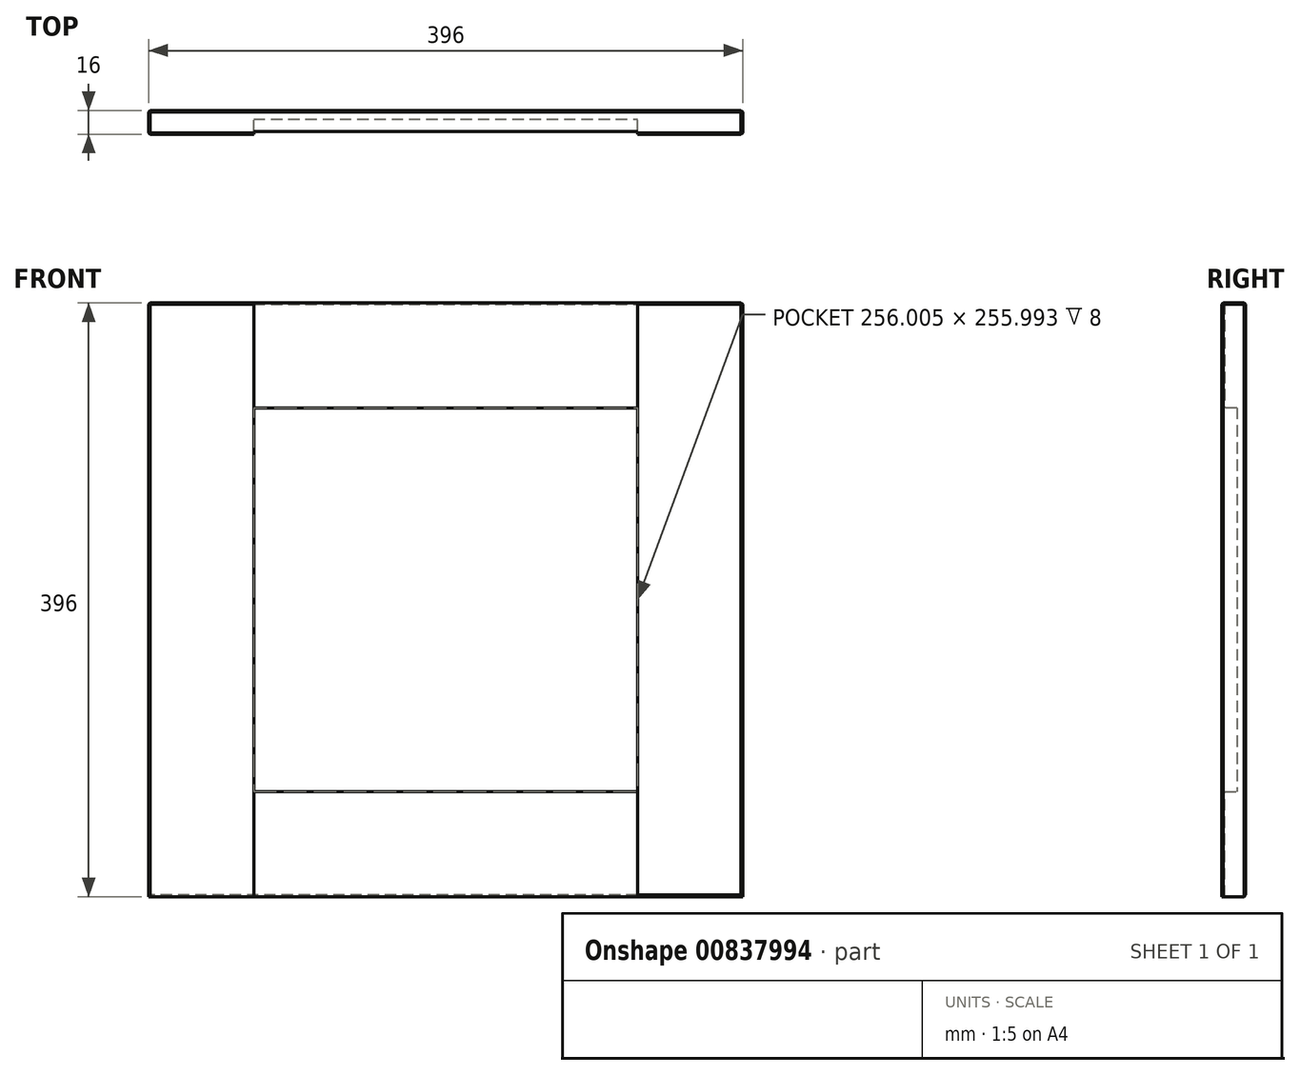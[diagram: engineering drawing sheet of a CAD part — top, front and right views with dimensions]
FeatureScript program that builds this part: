
annotation { "Feature Type Name" : "Feature", "Feature Type Description" : "" }
export const myFeature = defineFeature(function(context is Context, id is Id, definition is map)
    precondition{}
    {
        {
            var Q0;
            Q0=qCreatedBy(makeId("Front.planeOp"),FACE);
            var sketch = newSketch(context, id + "F0", { "sketchPlane" : qUnion([Q0])});
            skLineSegment(sketch, "E0.bottom", {"start": v(0, 0) * mm, "end": v(35.9, 0) * mm});
            skLineSegment(sketch, "E0.top", {"start": v(0, 30.12) * mm, "end": v(35.9, 30.12) * mm});
            skLineSegment(sketch, "E0.left", {"start": v(0, 0) * mm, "end": v(0, 30.12) * mm});
            skLineSegment(sketch, "E0.right", {"start": v(35.9, 0) * mm, "end": v(35.9, 30.12) * mm});
            skSolve(sketch);
        }
        {
            var Q0;
            Q0=makeQuery(id+"F0.imprint","IMPRINT",FACE,{"disambiguationData":[TD([[makeQuery(id+"F0.imprint","IMPRINT",EDGE,{"derivedFrom":sQuery(id+"F0.wireOp",EDGE,"E0.bottom")}),1.0]])]});
            extrude(context, id + "F1", {"entities" : qUnion([Q0]), "depth" : 16 * mm, "offsetDistance" : 25.4 * mm});
        }
        {
            var Q0;
            Q0=makeQuery(id+"F1.opExtrude","SWEPT_FACE",FACE,{"disambiguationData":[OSD([sQuery(id+"F0.wireOp",EDGE,"E0.left")])]});
            extrude(context, id + "F2", {"entities" : qUnion([Q0]), "operationType" : NewBodyOperationType.ADD, "oppositeDirection" : true, "depth" : 196 * mm, "offsetDistance" : 25 * mm});
        }
        {
            var Q0;
            {var subQ0=sQuery(id+"F0.wireOp",EDGE,"E0.bottom");Q0=makeQuery(id+"F2.boolean.opBoolean","MERGE",FACE,{"derivedFrom":[makeQuery(id+"F1.opExtrude","SWEPT_FACE",FACE,{"disambiguationData":[OSD([subQ0])]}),makeQuery(id+"F2.opExtrude","SWEPT_FACE",FACE,{"disambiguationData":[OSD([subQ0,sQuery(id+"F0.wireOp",EDGE,"E0.left")])]})]});}
            extrude(context, id + "F3", {"entities" : qUnion([Q0]), "operationType" : NewBodyOperationType.ADD, "oppositeDirection" : true, "depth" : 796 * mm, "offsetDistance" : 25 * mm});
        }
        {
            var Q0;
            {var subQ0=sQuery(id+"F0.wireOp",EDGE,"E0.left");var subQ1=sQuery(id+"F0.wireOp",EDGE,"E0.bottom");Q0=makeQuery(id+"F3.boolean.opBoolean","MERGE",FACE,{"derivedFrom":[makeQuery(id+"F2.boolean.opBoolean","MERGE",FACE,{"derivedFrom":[makeQuery(id+"F1.opExtrude","CAP_FACE",FACE,{"disambiguationData":[OSD([subQ1,sQuery(id+"F0.wireOp",EDGE,"E0.top"),subQ0,sQuery(id+"F0.wireOp",EDGE,"E0.right")])],"isStart":false}),makeQuery(id+"F2.opExtrude","SWEPT_FACE",FACE,{"disambiguationData":[OSD([subQ0]),TDD([makeQuery(id+"F1.opExtrude","CAP_EDGE",EDGE,{"disambiguationData":[OSD([subQ0])],"isStart":false})])]})]}),makeQuery(id+"F3.opExtrude","SWEPT_FACE",FACE,{"disambiguationData":[OSD([subQ1,subQ0]),TDD([makeQuery(id+"F2.boolean.opBoolean","MERGE",EDGE,{"derivedFrom":[makeQuery(id+"F1.opExtrude","CAP_EDGE",EDGE,{"disambiguationData":[OSD([subQ1])],"isStart":false}),makeQuery(id+"F2.opExtrude","SWEPT_EDGE",EDGE,{"disambiguationData":[OSD([subQ1,subQ0]),TDD([makeQuery(id+"F1.opExtrude","CAP_VERTEX",VERTEX,{"disambiguationData":[OSD([subQ1,subQ0])],"isStart":false})])]})]})])]})]});}
            var sketch = newSketch(context, id + "F4", { "sketchPlane" : qUnion([Q0])});
            skLineSegment(sketch, "E1.bottom", {"start": v(0, 796) * mm, "end": v(42.19, 796) * mm});
            skLineSegment(sketch, "E1.top", {"start": v(0, 751.57) * mm, "end": v(42.19, 751.57) * mm});
            skLineSegment(sketch, "E1.left", {"start": v(0, 796) * mm, "end": v(0, 751.57) * mm});
            skLineSegment(sketch, "E1.right", {"start": v(42.19, 796) * mm, "end": v(42.19, 751.57) * mm});
            skLineSegment(sketch, "E2.bottom", {"start": v(196, 796) * mm, "end": v(153.6, 796) * mm});
            skLineSegment(sketch, "E2.top", {"start": v(196, 746.75) * mm, "end": v(153.6, 746.75) * mm});
            skLineSegment(sketch, "E2.left", {"start": v(196, 796) * mm, "end": v(196, 746.75) * mm});
            skLineSegment(sketch, "E2.right", {"start": v(153.6, 796) * mm, "end": v(153.6, 746.75) * mm});
            skSolve(sketch);
        }
        {
            var Q0;
            Q0=makeQuery(id+"F4.imprint","IMPRINT",FACE,{"disambiguationData":[TD([[makeQuery(id+"F4.imprint","IMPRINT",EDGE,{"derivedFrom":sQuery(id+"F4.wireOp",EDGE,"E1.bottom")}),-1.0]])]});
            var Q1;
            Q1=makeQuery(id+"F4.imprint","IMPRINT",FACE,{"disambiguationData":[TD([[makeQuery(id+"F4.imprint","IMPRINT",EDGE,{"derivedFrom":sQuery(id+"F4.wireOp",EDGE,"E2.bottom")}),-1.0]])]});
            extrude(context, id + "F5", {"entities" : qUnion([Q0, Q1]), "operationType" : NewBodyOperationType.ADD, "depth" : 25 * mm, "offsetDistance" : 25 * mm});
        }
        {
            var Q0;
            {var subQ0=sQuery(id+"F0.wireOp",EDGE,"E0.left");var subQ1=sQuery(id+"F0.wireOp",EDGE,"E0.bottom");Q0=makeQuery(id+"F3.boolean.opBoolean","MERGE",FACE,{"derivedFrom":[makeQuery(id+"F2.boolean.opBoolean","MERGE",FACE,{"derivedFrom":[makeQuery(id+"F1.opExtrude","CAP_FACE",FACE,{"disambiguationData":[OSD([subQ1,sQuery(id+"F0.wireOp",EDGE,"E0.top"),subQ0,sQuery(id+"F0.wireOp",EDGE,"E0.right")])],"isStart":false}),makeQuery(id+"F2.opExtrude","SWEPT_FACE",FACE,{"disambiguationData":[OSD([subQ0]),TDD([makeQuery(id+"F1.opExtrude","CAP_EDGE",EDGE,{"disambiguationData":[OSD([subQ0])],"isStart":false})])]})]}),makeQuery(id+"F3.opExtrude","SWEPT_FACE",FACE,{"disambiguationData":[OSD([subQ1,subQ0]),TDD([makeQuery(id+"F2.boolean.opBoolean","MERGE",EDGE,{"derivedFrom":[makeQuery(id+"F1.opExtrude","CAP_EDGE",EDGE,{"disambiguationData":[OSD([subQ1])],"isStart":false}),makeQuery(id+"F2.opExtrude","SWEPT_EDGE",EDGE,{"disambiguationData":[OSD([subQ1,subQ0]),TDD([makeQuery(id+"F1.opExtrude","CAP_VERTEX",VERTEX,{"disambiguationData":[OSD([subQ1,subQ0])],"isStart":false})])]})]})])]})]});}
            var sketch = newSketch(context, id + "F6", { "sketchPlane" : qUnion([Q0])});
            skLineSegment(sketch, "E3.bottom", {"start": v(196, 0) * mm, "end": v(163.38, 0) * mm});
            skLineSegment(sketch, "E3.top", {"start": v(196, 46.55) * mm, "end": v(163.38, 46.55) * mm});
            skLineSegment(sketch, "E3.left", {"start": v(196, 0) * mm, "end": v(196, 46.55) * mm});
            skLineSegment(sketch, "E3.right", {"start": v(163.38, 0) * mm, "end": v(163.38, 46.55) * mm});
            skLineSegment(sketch, "E4.bottom", {"start": v(0, 0) * mm, "end": v(50.28, 0) * mm});
            skLineSegment(sketch, "E4.top", {"start": v(0, 44.4) * mm, "end": v(50.28, 44.4) * mm});
            skLineSegment(sketch, "E4.left", {"start": v(0, 0) * mm, "end": v(0, 44.4) * mm});
            skLineSegment(sketch, "E4.right", {"start": v(50.28, 0) * mm, "end": v(50.28, 44.4) * mm});
            skSolve(sketch);
        }
        {
            var Q0;
            Q0=makeQuery(id+"F6.imprint","IMPRINT",FACE,{"disambiguationData":[TD([[makeQuery(id+"F6.imprint","IMPRINT",EDGE,{"derivedFrom":sQuery(id+"F6.wireOp",EDGE,"E3.bottom")}),1.0]])]});
            var Q1;
            Q1=makeQuery(id+"F6.imprint","IMPRINT",FACE,{"disambiguationData":[TD([[makeQuery(id+"F6.imprint","IMPRINT",EDGE,{"derivedFrom":sQuery(id+"F6.wireOp",EDGE,"E4.bottom")}),1.0]])]});
            extrude(context, id + "F7", {"entities" : qUnion([Q0, Q1]), "operationType" : NewBodyOperationType.ADD, "depth" : 25 * mm, "offsetDistance" : 25 * mm});
        }
        {
            var Q0;
            Q0=makeQuery(id+"F7.opExtrude","SWEPT_FACE",FACE,{"disambiguationData":[OSD([sQuery(id+"F6.wireOp",EDGE,"E4.right")])]});
            extrude(context, id + "F8", {"entities" : qUnion([Q0]), "operationType" : NewBodyOperationType.ADD, "depth" : 19.72 * mm, "offsetDistance" : 25 * mm});
        }
        {
            var Q0;
            {var subQ0=sQuery(id+"F6.wireOp",EDGE,"E4.top");Q0=makeQuery(id+"F8.boolean.opBoolean","MERGE",FACE,{"derivedFrom":[makeQuery(id+"F7.opExtrude","SWEPT_FACE",FACE,{"disambiguationData":[OSD([subQ0])]}),makeQuery(id+"F8.opExtrude","SWEPT_FACE",FACE,{"disambiguationData":[OSD([subQ0,sQuery(id+"F6.wireOp",EDGE,"E4.right")])]})]});}
            extrude(context, id + "F9", {"entities" : qUnion([Q0]), "operationType" : NewBodyOperationType.ADD, "depth" : 25.6 * mm, "offsetDistance" : 25 * mm});
        }
        {
            var Q0;
            Q0=makeQuery(id+"F7.opExtrude","SWEPT_FACE",FACE,{"disambiguationData":[OSD([sQuery(id+"F6.wireOp",EDGE,"E3.right")])]});
            extrude(context, id + "F10", {"entities" : qUnion([Q0]), "operationType" : NewBodyOperationType.ADD, "depth" : 37.38 * mm, "offsetDistance" : 25 * mm});
        }
        {
            var Q0;
            {var subQ0=sQuery(id+"F6.wireOp",EDGE,"E3.top");Q0=makeQuery(id+"F10.boolean.opBoolean","MERGE",FACE,{"derivedFrom":[makeQuery(id+"F7.opExtrude","SWEPT_FACE",FACE,{"disambiguationData":[OSD([subQ0])]}),makeQuery(id+"F10.opExtrude","SWEPT_FACE",FACE,{"disambiguationData":[OSD([subQ0,sQuery(id+"F6.wireOp",EDGE,"E3.right")])]})]});}
            extrude(context, id + "F11", {"entities" : qUnion([Q0]), "operationType" : NewBodyOperationType.ADD, "depth" : 23.45 * mm, "offsetDistance" : 25 * mm});
        }
        {
            var Q0;
            Q0=makeQuery(id+"F5.opExtrude","SWEPT_FACE",FACE,{"disambiguationData":[OSD([sQuery(id+"F4.wireOp",EDGE,"E1.right")])]});
            extrude(context, id + "F12", {"entities" : qUnion([Q0]), "operationType" : NewBodyOperationType.ADD, "depth" : 27.8 * mm, "offsetDistance" : 25 * mm});
        }
        {
            var Q0;
            {var subQ0=sQuery(id+"F4.wireOp",EDGE,"E1.top");Q0=makeQuery(id+"F12.boolean.opBoolean","MERGE",FACE,{"derivedFrom":[makeQuery(id+"F5.opExtrude","SWEPT_FACE",FACE,{"disambiguationData":[OSD([subQ0])]}),makeQuery(id+"F12.opExtrude","SWEPT_FACE",FACE,{"disambiguationData":[OSD([subQ0,sQuery(id+"F4.wireOp",EDGE,"E1.right")])]})]});}
            extrude(context, id + "F13", {"entities" : qUnion([Q0]), "operationType" : NewBodyOperationType.ADD, "depth" : 25.57 * mm, "offsetDistance" : 25 * mm});
        }
        {
            var Q0;
            Q0=makeQuery(id+"F5.opExtrude","SWEPT_FACE",FACE,{"disambiguationData":[OSD([sQuery(id+"F4.wireOp",EDGE,"E2.top")])]});
            extrude(context, id + "F14", {"entities" : qUnion([Q0]), "operationType" : NewBodyOperationType.ADD, "depth" : 20.75 * mm, "offsetDistance" : 25 * mm});
        }
        {
            var Q0;
            {var subQ0=sQuery(id+"F4.wireOp",EDGE,"E2.right");Q0=makeQuery(id+"F14.boolean.opBoolean","MERGE",FACE,{"derivedFrom":[makeQuery(id+"F5.opExtrude","SWEPT_FACE",FACE,{"disambiguationData":[OSD([subQ0])]}),makeQuery(id+"F14.opExtrude","SWEPT_FACE",FACE,{"disambiguationData":[OSD([sQuery(id+"F4.wireOp",EDGE,"E2.top"),subQ0])]})]});}
            extrude(context, id + "F15", {"entities" : qUnion([Q0]), "operationType" : NewBodyOperationType.ADD, "depth" : 27.6 * mm, "offsetDistance" : 25 * mm});
        }
        {
            var Q0;
            {var subQ0=sQuery(id+"F0.wireOp",EDGE,"E0.left");var subQ1=sQuery(id+"F0.wireOp",EDGE,"E0.bottom");Q0=makeQuery(id+"F3.boolean.opBoolean","MERGE",FACE,{"derivedFrom":[makeQuery(id+"F2.boolean.opBoolean","MERGE",FACE,{"derivedFrom":[makeQuery(id+"F1.opExtrude","CAP_FACE",FACE,{"disambiguationData":[OSD([subQ1,sQuery(id+"F0.wireOp",EDGE,"E0.top"),subQ0,sQuery(id+"F0.wireOp",EDGE,"E0.right")])],"isStart":false}),makeQuery(id+"F2.opExtrude","SWEPT_FACE",FACE,{"disambiguationData":[OSD([subQ0]),TDD([makeQuery(id+"F1.opExtrude","CAP_EDGE",EDGE,{"disambiguationData":[OSD([subQ0])],"isStart":false})])]})]}),makeQuery(id+"F3.opExtrude","SWEPT_FACE",FACE,{"disambiguationData":[OSD([subQ1,subQ0]),TDD([makeQuery(id+"F2.boolean.opBoolean","MERGE",EDGE,{"derivedFrom":[makeQuery(id+"F1.opExtrude","CAP_EDGE",EDGE,{"disambiguationData":[OSD([subQ1])],"isStart":false}),makeQuery(id+"F2.opExtrude","SWEPT_EDGE",EDGE,{"disambiguationData":[OSD([subQ1,subQ0]),TDD([makeQuery(id+"F1.opExtrude","CAP_VERTEX",VERTEX,{"disambiguationData":[OSD([subQ1,subQ0])],"isStart":false})])]})]})])]})]});}
            var sketch = newSketch(context, id + "F16", { "sketchPlane" : qUnion([Q0])});
            skLineSegment(sketch, "E5.bottom", {"start": v(70, 726) * mm, "end": v(126, 726) * mm});
            skLineSegment(sketch, "E5.top", {"start": v(70, 70) * mm, "end": v(126, 70) * mm});
            skLineSegment(sketch, "E5.left", {"start": v(70, 726) * mm, "end": v(70, 70) * mm});
            skLineSegment(sketch, "E5.right", {"start": v(126, 726) * mm, "end": v(126, 70) * mm});
            skSolve(sketch);
        }
        {
            var Q0;
            Q0=makeQuery(id+"F16.imprint","IMPRINT",FACE,{"disambiguationData":[TD([[makeQuery(id+"F16.imprint","IMPRINT",EDGE,{"derivedFrom":sQuery(id+"F16.wireOp",EDGE,"E5.top")}),1.0]])]});
            extrude(context, id + "F17", {"entities" : qUnion([Q0]), "operationType" : NewBodyOperationType.REMOVE, "oppositeDirection" : true, "depth" : 10 * mm, "offsetDistance" : 25 * mm});
        }
        {
            var Q0;
            {var subQ2=sQuery(id+"F0.wireOp",EDGE,"E0.left");var subQ3=sQuery(id+"F0.wireOp",EDGE,"E0.bottom");var subQ4=makeQuery(id+"F1.opExtrude","CAP_FACE",FACE,{"disambiguationData":[OSD([subQ3,sQuery(id+"F0.wireOp",EDGE,"E0.top"),subQ2,sQuery(id+"F0.wireOp",EDGE,"E0.right")])],"isStart":false});var subQ7=makeQuery(id+"F3.opExtrude","SWEPT_FACE",FACE,{"disambiguationData":[OSD([subQ3,subQ2]),TDD([makeQuery(id+"F2.boolean.opBoolean","MERGE",EDGE,{"derivedFrom":[makeQuery(id+"F1.opExtrude","CAP_EDGE",EDGE,{"disambiguationData":[OSD([subQ3])],"isStart":false}),makeQuery(id+"F2.opExtrude","SWEPT_EDGE",EDGE,{"disambiguationData":[OSD([subQ3,subQ2]),TDD([makeQuery(id+"F1.opExtrude","CAP_VERTEX",VERTEX,{"disambiguationData":[OSD([subQ3,subQ2])],"isStart":false})])]})]})])]});var subQ8=makeQuery(id+"F2.opExtrude","SWEPT_FACE",FACE,{"disambiguationData":[OSD([subQ2]),TDD([makeQuery(id+"F1.opExtrude","CAP_EDGE",EDGE,{"disambiguationData":[OSD([subQ2])],"isStart":false})])]});Q0=makeQuery(id+"F17.boolean.opBoolean","SPLIT",FACE,{"disambiguationData":[TD([makeQuery(id+"F1.opExtrude","SWEPT_FACE",FACE,{"disambiguationData":[OSD([subQ3])]})])],"derivedFrom":makeQuery(id+"F3.boolean.opBoolean","MERGE",FACE,{"derivedFrom":[makeQuery(id+"F2.boolean.opBoolean","MERGE",FACE,{"derivedFrom":[subQ4,subQ8]}),subQ7]})});}
            var Q1;
            {var subQ2=sQuery(id+"F4.wireOp",EDGE,"E1.bottom");var subQ3=sQuery(id+"F0.wireOp",EDGE,"E0.left");var subQ4=sQuery(id+"F0.wireOp",EDGE,"E0.bottom");var subQ6=makeQuery(id+"F1.opExtrude","CAP_FACE",FACE,{"disambiguationData":[OSD([subQ4,sQuery(id+"F0.wireOp",EDGE,"E0.top"),subQ3,sQuery(id+"F0.wireOp",EDGE,"E0.right")])],"isStart":false});var subQ7=makeQuery(id+"F2.opExtrude","SWEPT_FACE",FACE,{"disambiguationData":[OSD([subQ3]),TDD([makeQuery(id+"F1.opExtrude","CAP_EDGE",EDGE,{"disambiguationData":[OSD([subQ3])],"isStart":false})])]});var subQ8=makeQuery(id+"F3.opExtrude","SWEPT_FACE",FACE,{"disambiguationData":[OSD([subQ4,subQ3]),TDD([makeQuery(id+"F2.boolean.opBoolean","MERGE",EDGE,{"derivedFrom":[makeQuery(id+"F1.opExtrude","CAP_EDGE",EDGE,{"disambiguationData":[OSD([subQ4])],"isStart":false}),makeQuery(id+"F2.opExtrude","SWEPT_EDGE",EDGE,{"disambiguationData":[OSD([subQ4,subQ3]),TDD([makeQuery(id+"F1.opExtrude","CAP_VERTEX",VERTEX,{"disambiguationData":[OSD([subQ4,subQ3])],"isStart":false})])]})]})])]});Q1=makeQuery(id+"F17.boolean.opBoolean","SPLIT",FACE,{"disambiguationData":[TD([makeQuery(id+"F5.opExtrude","SWEPT_FACE",FACE,{"disambiguationData":[OSD([subQ2])]})])],"derivedFrom":makeQuery(id+"F3.boolean.opBoolean","MERGE",FACE,{"derivedFrom":[makeQuery(id+"F2.boolean.opBoolean","MERGE",FACE,{"derivedFrom":[subQ6,subQ7]}),subQ8]})});}
            extrude(context, id + "F18", {"entities" : qUnion([Q0, Q1]), "operationType" : NewBodyOperationType.REMOVE, "oppositeDirection" : true, "depth" : 2 * mm, "offsetDistance" : 25 * mm});
        }
        {
            var Q0;
            {var subQ0=sQuery(id+"F4.wireOp",EDGE,"E1.right");var subQ1=sQuery(id+"F4.wireOp",EDGE,"E1.top");Q0=makeQuery(id+"F13.boolean.opBoolean","MERGE",FACE,{"derivedFrom":[makeQuery(id+"F12.boolean.opBoolean","MERGE",FACE,{"derivedFrom":[makeQuery(id+"F5.opExtrude","CAP_FACE",FACE,{"disambiguationData":[OSD([sQuery(id+"F4.wireOp",EDGE,"E1.bottom"),subQ1,sQuery(id+"F4.wireOp",EDGE,"E1.left"),subQ0])],"isStart":false}),makeQuery(id+"F12.opExtrude","SWEPT_FACE",FACE,{"disambiguationData":[OSD([subQ0]),TDD([makeQuery(id+"F5.opExtrude","CAP_EDGE",EDGE,{"disambiguationData":[OSD([subQ0])],"isStart":false})])]})]}),makeQuery(id+"F13.opExtrude","SWEPT_FACE",FACE,{"disambiguationData":[OSD([subQ1,subQ0]),TDD([makeQuery(id+"F12.boolean.opBoolean","MERGE",EDGE,{"derivedFrom":[makeQuery(id+"F5.opExtrude","CAP_EDGE",EDGE,{"disambiguationData":[OSD([subQ1])],"isStart":false}),makeQuery(id+"F12.opExtrude","SWEPT_EDGE",EDGE,{"disambiguationData":[OSD([subQ1,subQ0]),TDD([makeQuery(id+"F5.opExtrude","CAP_VERTEX",VERTEX,{"disambiguationData":[OSD([subQ1,subQ0])],"isStart":false})])]})]})])]})]});}
            var Q1;
            {var subQ0=sQuery(id+"F4.wireOp",EDGE,"E2.right");var subQ1=sQuery(id+"F4.wireOp",EDGE,"E2.top");Q1=makeQuery(id+"F15.boolean.opBoolean","MERGE",FACE,{"derivedFrom":[makeQuery(id+"F14.boolean.opBoolean","MERGE",FACE,{"derivedFrom":[makeQuery(id+"F5.opExtrude","CAP_FACE",FACE,{"disambiguationData":[OSD([sQuery(id+"F4.wireOp",EDGE,"E2.bottom"),subQ1,sQuery(id+"F4.wireOp",EDGE,"E2.left"),subQ0])],"isStart":false}),makeQuery(id+"F14.opExtrude","SWEPT_FACE",FACE,{"disambiguationData":[OSD([subQ1]),TDD([makeQuery(id+"F5.opExtrude","CAP_EDGE",EDGE,{"disambiguationData":[OSD([subQ1])],"isStart":false})])]})]}),makeQuery(id+"F15.opExtrude","SWEPT_FACE",FACE,{"disambiguationData":[OSD([subQ1,subQ0]),TDD([makeQuery(id+"F14.boolean.opBoolean","MERGE",EDGE,{"derivedFrom":[makeQuery(id+"F5.opExtrude","CAP_EDGE",EDGE,{"disambiguationData":[OSD([subQ0])],"isStart":false}),makeQuery(id+"F14.opExtrude","SWEPT_EDGE",EDGE,{"disambiguationData":[OSD([subQ1,subQ0]),TDD([makeQuery(id+"F5.opExtrude","CAP_VERTEX",VERTEX,{"disambiguationData":[OSD([subQ1,subQ0])],"isStart":false})])]})]})])]})]});}
            var Q2;
            {var subQ0=sQuery(id+"F6.wireOp",EDGE,"E4.right");var subQ1=sQuery(id+"F6.wireOp",EDGE,"E4.top");Q2=makeQuery(id+"F9.boolean.opBoolean","MERGE",FACE,{"derivedFrom":[makeQuery(id+"F8.boolean.opBoolean","MERGE",FACE,{"derivedFrom":[makeQuery(id+"F7.opExtrude","CAP_FACE",FACE,{"disambiguationData":[OSD([sQuery(id+"F6.wireOp",EDGE,"E4.bottom"),subQ1,sQuery(id+"F6.wireOp",EDGE,"E4.left"),subQ0])],"isStart":false}),makeQuery(id+"F8.opExtrude","SWEPT_FACE",FACE,{"disambiguationData":[OSD([subQ0]),TDD([makeQuery(id+"F7.opExtrude","CAP_EDGE",EDGE,{"disambiguationData":[OSD([subQ0])],"isStart":false})])]})]}),makeQuery(id+"F9.opExtrude","SWEPT_FACE",FACE,{"disambiguationData":[OSD([subQ1,subQ0]),TDD([makeQuery(id+"F8.boolean.opBoolean","MERGE",EDGE,{"derivedFrom":[makeQuery(id+"F7.opExtrude","CAP_EDGE",EDGE,{"disambiguationData":[OSD([subQ1])],"isStart":false}),makeQuery(id+"F8.opExtrude","SWEPT_EDGE",EDGE,{"disambiguationData":[OSD([subQ1,subQ0]),TDD([makeQuery(id+"F7.opExtrude","CAP_VERTEX",VERTEX,{"disambiguationData":[OSD([subQ1,subQ0])],"isStart":false})])]})]})])]})]});}
            var Q3;
            {var subQ0=sQuery(id+"F6.wireOp",EDGE,"E3.right");var subQ1=sQuery(id+"F6.wireOp",EDGE,"E3.top");Q3=makeQuery(id+"F11.boolean.opBoolean","MERGE",FACE,{"derivedFrom":[makeQuery(id+"F10.boolean.opBoolean","MERGE",FACE,{"derivedFrom":[makeQuery(id+"F7.opExtrude","CAP_FACE",FACE,{"disambiguationData":[OSD([sQuery(id+"F6.wireOp",EDGE,"E3.bottom"),subQ1,sQuery(id+"F6.wireOp",EDGE,"E3.left"),subQ0])],"isStart":false}),makeQuery(id+"F10.opExtrude","SWEPT_FACE",FACE,{"disambiguationData":[OSD([subQ0]),TDD([makeQuery(id+"F7.opExtrude","CAP_EDGE",EDGE,{"disambiguationData":[OSD([subQ0])],"isStart":false})])]})]}),makeQuery(id+"F11.opExtrude","SWEPT_FACE",FACE,{"disambiguationData":[OSD([subQ1,subQ0]),TDD([makeQuery(id+"F10.boolean.opBoolean","MERGE",EDGE,{"derivedFrom":[makeQuery(id+"F7.opExtrude","CAP_EDGE",EDGE,{"disambiguationData":[OSD([subQ1])],"isStart":false}),makeQuery(id+"F10.opExtrude","SWEPT_EDGE",EDGE,{"disambiguationData":[OSD([subQ1,subQ0]),TDD([makeQuery(id+"F7.opExtrude","CAP_VERTEX",VERTEX,{"disambiguationData":[OSD([subQ1,subQ0])],"isStart":false})])]})]})])]})]});}
            extrude(context, id + "F19", {"entities" : qUnion([Q0, Q1, Q2, Q3]), "operationType" : NewBodyOperationType.REMOVE, "oppositeDirection" : true, "depth" : 25 * mm, "offsetDistance" : 25 * mm});
        }
        {
            var Q0;
            {var subQ0=sQuery(id+"F4.wireOp",EDGE,"E2.left");var subQ1=sQuery(id+"F0.wireOp",EDGE,"E0.left");var subQ2=sQuery(id+"F0.wireOp",EDGE,"E0.bottom");var subQ3=sQuery(id+"F6.wireOp",EDGE,"E3.left");Q0=makeQuery(id+"F14.boolean.opBoolean","MERGE",FACE,{"derivedFrom":[makeQuery(id+"F11.boolean.opBoolean","MERGE",FACE,{"derivedFrom":[makeQuery(id+"F7.boolean.opBoolean","MERGE",FACE,{"derivedFrom":[makeQuery(id+"F5.boolean.opBoolean","MERGE",FACE,{"derivedFrom":[makeQuery(id+"F3.boolean.opBoolean","MERGE",FACE,{"derivedFrom":[makeQuery(id+"F2.opExtrude","CAP_FACE",FACE,{"disambiguationData":[OSD([subQ1])],"isStart":false}),makeQuery(id+"F3.opExtrude","SWEPT_FACE",FACE,{"disambiguationData":[OSD([subQ2,subQ1]),TDD([makeQuery(id+"F2.opExtrude","CAP_EDGE",EDGE,{"disambiguationData":[OSD([subQ2,subQ1])],"isStart":false})])]})]}),makeQuery(id+"F5.opExtrude","SWEPT_FACE",FACE,{"disambiguationData":[OSD([subQ0])]})]}),makeQuery(id+"F7.opExtrude","SWEPT_FACE",FACE,{"disambiguationData":[OSD([subQ3])]})]}),makeQuery(id+"F11.opExtrude","SWEPT_FACE",FACE,{"disambiguationData":[OSD([subQ2,subQ1,sQuery(id+"F6.wireOp",EDGE,"E3.top"),subQ3])]})]}),makeQuery(id+"F14.opExtrude","SWEPT_FACE",FACE,{"disambiguationData":[OSD([subQ2,subQ1,sQuery(id+"F4.wireOp",EDGE,"E2.top"),subQ0])]})]});}
            extrude(context, id + "F20", {"entities" : qUnion([Q0]), "operationType" : NewBodyOperationType.ADD, "depth" : 200 * mm, "offsetDistance" : 25 * mm});
        }
        {
            var Q0;
            {var subQ0=sQuery(id+"F4.wireOp",EDGE,"E2.right");var subQ1=sQuery(id+"F4.wireOp",EDGE,"E2.top");Q0=makeQuery(id+"F18.boolean.opBoolean","MERGE",FACE,{"derivedFrom":[makeQuery(id+"F15.opExtrude","CAP_FACE",FACE,{"disambiguationData":[OSD([subQ1,subQ0])],"isStart":false}),makeQuery(id+"F18.opExtrude","SWEPT_FACE",FACE,{"disambiguationData":[OSD([subQ1,subQ0])]})]});}
            var Q1;
            {var subQ0=sQuery(id+"F6.wireOp",EDGE,"E3.right");var subQ1=sQuery(id+"F6.wireOp",EDGE,"E3.top");Q1=makeQuery(id+"F18.boolean.opBoolean","MERGE",FACE,{"derivedFrom":[makeQuery(id+"F11.boolean.opBoolean","MERGE",FACE,{"derivedFrom":[makeQuery(id+"F10.opExtrude","CAP_FACE",FACE,{"disambiguationData":[OSD([subQ0])],"isStart":false}),makeQuery(id+"F11.opExtrude","SWEPT_FACE",FACE,{"disambiguationData":[OSD([subQ1,subQ0]),TDD([makeQuery(id+"F10.opExtrude","CAP_EDGE",EDGE,{"disambiguationData":[OSD([subQ1,subQ0])],"isStart":false})])]})]}),makeQuery(id+"F17.boolean.opBoolean","COPY",FACE,{"derivedFrom":makeQuery(id+"F17.opExtrude","SWEPT_FACE",FACE,{"disambiguationData":[OSD([sQuery(id+"F16.wireOp",EDGE,"E5.right")])]})}),makeQuery(id+"F18.opExtrude","SWEPT_FACE",FACE,{"disambiguationData":[OSD([subQ1,subQ0])]})]});}
            extrude(context, id + "F21", {"entities" : qUnion([Q0, Q1]), "operationType" : NewBodyOperationType.REMOVE, "oppositeDirection" : true, "depth" : 200 * mm, "offsetDistance" : 25 * mm});
        }
        {
            var Q0;
            {var subQ0=sQuery(id+"F4.wireOp",EDGE,"E2.bottom");var subQ1=sQuery(id+"F0.wireOp",EDGE,"E0.left");var subQ2=sQuery(id+"F0.wireOp",EDGE,"E0.bottom");var subQ3=sQuery(id+"F4.wireOp",EDGE,"E1.bottom");Q0=makeQuery(id+"F20.boolean.opBoolean","MERGE",FACE,{"derivedFrom":[makeQuery(id+"F15.boolean.opBoolean","MERGE",FACE,{"derivedFrom":[makeQuery(id+"F12.boolean.opBoolean","MERGE",FACE,{"derivedFrom":[makeQuery(id+"F5.boolean.opBoolean","MERGE",FACE,{"derivedFrom":[makeQuery(id+"F3.opExtrude","CAP_FACE",FACE,{"disambiguationData":[OSD([subQ2,subQ1])],"isStart":false}),makeQuery(id+"F5.opExtrude","SWEPT_FACE",FACE,{"disambiguationData":[OSD([subQ3])]}),makeQuery(id+"F5.opExtrude","SWEPT_FACE",FACE,{"disambiguationData":[OSD([subQ0])]})]}),makeQuery(id+"F12.opExtrude","SWEPT_FACE",FACE,{"disambiguationData":[OSD([subQ2,subQ1,subQ3,sQuery(id+"F4.wireOp",EDGE,"E1.right")])]})]}),makeQuery(id+"F15.opExtrude","SWEPT_FACE",FACE,{"disambiguationData":[OSD([subQ2,subQ1,subQ0,sQuery(id+"F4.wireOp",EDGE,"E2.right")])]})]}),makeQuery(id+"F20.opExtrude","SWEPT_FACE",FACE,{"disambiguationData":[OSD([subQ2,subQ1,subQ0,sQuery(id+"F4.wireOp",EDGE,"E2.left")])]})]});}
            extrude(context, id + "F22", {"entities" : qUnion([Q0]), "operationType" : NewBodyOperationType.ADD, "depth" : 200 * mm, "offsetDistance" : 25 * mm});
        }
        {
            var Q0;
            Q0=makeQuery(id+"F17.boolean.opBoolean","COPY",FACE,{"derivedFrom":makeQuery(id+"F17.opExtrude","SWEPT_FACE",FACE,{"disambiguationData":[OSD([sQuery(id+"F16.wireOp",EDGE,"E5.bottom")])]})});
            var Q1;
            {var subQ0=sQuery(id+"F16.wireOp",EDGE,"E5.right");var subQ1=sQuery(id+"F16.wireOp",EDGE,"E5.bottom");var subQ2=sQuery(id+"F4.wireOp",EDGE,"E2.right");var subQ3=sQuery(id+"F4.wireOp",EDGE,"E2.top");var subQ4=makeQuery(id+"F17.boolean.opBoolean","COPY",EDGE,{"derivedFrom":makeQuery(id+"F17.opExtrude","SWEPT_EDGE",EDGE,{"disambiguationData":[OSD([subQ3,subQ2,subQ1,subQ0])]})});Q1=makeQuery(id+"F21.boolean.opBoolean","COPY",FACE,{"derivedFrom":makeQuery(id+"F21.opExtrude","SWEPT_FACE",FACE,{"disambiguationData":[OSD([subQ3,subQ2,subQ1,subQ0]),TDD([makeQuery(id+"F18.boolean.opBoolean","MERGE",EDGE,{"derivedFrom":[subQ4,makeQuery(id+"F18.opExtrude","SWEPT_EDGE",EDGE,{"disambiguationData":[OSD([subQ3,subQ2,subQ1,subQ0])]})]}),makeQuery(id+"F18.boolean.opBoolean","SPLIT",EDGE,{"derivedFrom":subQ4})])]})});}
            extrude(context, id + "F23", {"entities" : qUnion([Q0, Q1]), "operationType" : NewBodyOperationType.REMOVE, "oppositeDirection" : true, "depth" : 200 * mm, "offsetDistance" : 25 * mm});
        }
        {
            var Q0;
            Q0=makeQuery(id+"F23.boolean.opBoolean","COPY",FACE,{"derivedFrom":makeQuery(id+"F23.opExtrude","CAP_FACE",FACE,{"disambiguationData":[OSD([sQuery(id+"F16.wireOp",EDGE,"E5.bottom")])],"isStart":false})});
            var Q1;
            Q1=makeQuery(id+"F23.boolean.opBoolean","COPY",FACE,{"derivedFrom":makeQuery(id+"F23.opExtrude","CAP_FACE",FACE,{"disambiguationData":[OSD([sQuery(id+"F4.wireOp",EDGE,"E2.top"),sQuery(id+"F4.wireOp",EDGE,"E2.right"),sQuery(id+"F16.wireOp",EDGE,"E5.bottom"),sQuery(id+"F16.wireOp",EDGE,"E5.right")])],"isStart":false})});
            extrude(context, id + "F24", {"entities" : qUnion([Q0, Q1]), "operationType" : NewBodyOperationType.ADD, "depth" : 600 * mm, "offsetDistance" : 25 * mm});
        }
        {
            var Q0;
            Q0=makeQuery(id+"F22.opExtrude","CAP_FACE",FACE,{"disambiguationData":[OSD([sQuery(id+"F0.wireOp",EDGE,"E0.bottom"),sQuery(id+"F0.wireOp",EDGE,"E0.left"),sQuery(id+"F4.wireOp",EDGE,"E1.bottom"),sQuery(id+"F4.wireOp",EDGE,"E1.right"),sQuery(id+"F4.wireOp",EDGE,"E2.bottom"),sQuery(id+"F4.wireOp",EDGE,"E2.left"),sQuery(id+"F4.wireOp",EDGE,"E2.right")])],"isStart":false});
            extrude(context, id + "F25", {"entities" : qUnion([Q0]), "operationType" : NewBodyOperationType.REMOVE, "oppositeDirection" : true, "depth" : 600 * mm, "offsetDistance" : 25 * mm, "hasDraft" : true, "draftAngle" : 3 * degree});
        }
        {
            var Q0;
            {var subQ0=sQuery(id+"F4.wireOp",EDGE,"E1.right");var subQ1=sQuery(id+"F4.wireOp",EDGE,"E1.bottom");var subQ2=sQuery(id+"F0.wireOp",EDGE,"E0.left");var subQ3=sQuery(id+"F0.wireOp",EDGE,"E0.bottom");var subQ4=sQuery(id+"F4.wireOp",EDGE,"E1.left");var subQ5=sQuery(id+"F4.wireOp",EDGE,"E1.top");var subQ6=sQuery(id+"F6.wireOp",EDGE,"E4.right");var subQ7=sQuery(id+"F6.wireOp",EDGE,"E4.left");var subQ8=sQuery(id+"F6.wireOp",EDGE,"E4.top");var subQ9=makeQuery(id+"F1.opExtrude","CAP_FACE",FACE,{"disambiguationData":[OSD([subQ3,sQuery(id+"F0.wireOp",EDGE,"E0.top"),subQ2,sQuery(id+"F0.wireOp",EDGE,"E0.right")])],"isStart":false});var subQ10=makeQuery(id+"F3.opExtrude","SWEPT_FACE",FACE,{"disambiguationData":[OSD([subQ3,subQ2]),TDD([makeQuery(id+"F2.boolean.opBoolean","MERGE",EDGE,{"derivedFrom":[makeQuery(id+"F1.opExtrude","CAP_EDGE",EDGE,{"disambiguationData":[OSD([subQ3])],"isStart":false}),makeQuery(id+"F2.opExtrude","SWEPT_EDGE",EDGE,{"disambiguationData":[OSD([subQ3,subQ2]),TDD([makeQuery(id+"F1.opExtrude","CAP_VERTEX",VERTEX,{"disambiguationData":[OSD([subQ3,subQ2])],"isStart":false})])]})]})])]});var subQ11=makeQuery(id+"F2.opExtrude","SWEPT_FACE",FACE,{"disambiguationData":[OSD([subQ2]),TDD([makeQuery(id+"F1.opExtrude","CAP_EDGE",EDGE,{"disambiguationData":[OSD([subQ2])],"isStart":false})])]});Q0=makeQuery(id+"F25.boolean.opBoolean","INTERSECT",EDGE,{"derivedFrom":[makeQuery(id+"F22.boolean.opBoolean","MERGE",FACE,{"derivedFrom":[makeQuery(id+"F19.boolean.opBoolean","MERGE",FACE,{"derivedFrom":[makeQuery(id+"F17.boolean.opBoolean","SPLIT",FACE,{"disambiguationData":[TD([makeQuery(id+"F1.opExtrude","SWEPT_FACE",FACE,{"disambiguationData":[OSD([subQ2])]})])],"derivedFrom":makeQuery(id+"F3.boolean.opBoolean","MERGE",FACE,{"derivedFrom":[makeQuery(id+"F2.boolean.opBoolean","MERGE",FACE,{"derivedFrom":[subQ9,subQ11]}),subQ10]})}),makeQuery(id+"F19.opExtrude","CAP_FACE",FACE,{"disambiguationData":[OSD([sQuery(id+"F6.wireOp",EDGE,"E4.bottom"),subQ8,subQ7,subQ6])],"isStart":false}),makeQuery(id+"F19.opExtrude","CAP_FACE",FACE,{"disambiguationData":[OSD([subQ1,subQ5,subQ4,subQ0])],"isStart":false})]}),makeQuery(id+"F22.opExtrude","SWEPT_FACE",FACE,{"disambiguationData":[OSD([subQ3,subQ2,subQ1,subQ0]),TDD([makeQuery(id+"F19.boolean.opBoolean","COPY",EDGE,{"derivedFrom":makeQuery(id+"F19.opExtrude","CAP_EDGE",EDGE,{"disambiguationData":[OSD([subQ3,subQ2,subQ1,subQ0])],"isStart":false})})])]})]}),makeQuery(id+"F25.opExtrude","CAP_FACE",FACE,{"disambiguationData":[OSD([subQ3,subQ2,subQ1,subQ0,sQuery(id+"F4.wireOp",EDGE,"E2.bottom"),sQuery(id+"F4.wireOp",EDGE,"E2.left"),sQuery(id+"F4.wireOp",EDGE,"E2.right")])],"isStart":false})]});}
            var Q1;
            {var subQ0=sQuery(id+"F4.wireOp",EDGE,"E1.left");var subQ1=sQuery(id+"F0.wireOp",EDGE,"E0.left");var subQ2=sQuery(id+"F0.wireOp",EDGE,"E0.bottom");Q1=makeQuery(id+"F22.boolean.opBoolean","MERGE",EDGE,{"derivedFrom":[makeQuery(id+"F19.boolean.opBoolean","MERGE",EDGE,{"derivedFrom":[makeQuery(id+"F3.boolean.opBoolean","MERGE",EDGE,{"derivedFrom":[makeQuery(id+"F1.opExtrude","CAP_EDGE",EDGE,{"disambiguationData":[OSD([subQ1])],"isStart":false}),makeQuery(id+"F3.opExtrude","SWEPT_EDGE",EDGE,{"disambiguationData":[OSD([subQ2,subQ1]),TDD([makeQuery(id+"F1.opExtrude","CAP_VERTEX",VERTEX,{"disambiguationData":[OSD([subQ2,subQ1])],"isStart":false})])]})]}),makeQuery(id+"F19.opExtrude","CAP_EDGE",EDGE,{"disambiguationData":[OSD([subQ2,subQ1,sQuery(id+"F6.wireOp",EDGE,"E4.top"),sQuery(id+"F6.wireOp",EDGE,"E4.left")])],"isStart":false}),makeQuery(id+"F19.opExtrude","CAP_EDGE",EDGE,{"disambiguationData":[OSD([subQ2,subQ1,sQuery(id+"F4.wireOp",EDGE,"E1.top"),subQ0])],"isStart":false})]}),makeQuery(id+"F22.opExtrude","SWEPT_EDGE",EDGE,{"disambiguationData":[OSD([sQuery(id+"F4.wireOp",EDGE,"E1.bottom"),subQ0])]})]});}
            var Q2;
            Q2=makeQuery(id+"F19.boolean.opBoolean","COPY",EDGE,{"derivedFrom":makeQuery(id+"F19.opExtrude","CAP_EDGE",EDGE,{"disambiguationData":[OSD([sQuery(id+"F0.wireOp",EDGE,"E0.bottom"),sQuery(id+"F0.wireOp",EDGE,"E0.left"),sQuery(id+"F6.wireOp",EDGE,"E4.bottom"),sQuery(id+"F6.wireOp",EDGE,"E4.right")])],"isStart":false})});
            var Q3;
            {var subQ0=sQuery(id+"F6.wireOp",EDGE,"E3.bottom");Q3=makeQuery(id+"F20.boolean.opBoolean","MERGE",EDGE,{"derivedFrom":[makeQuery(id+"F19.boolean.opBoolean","COPY",EDGE,{"derivedFrom":makeQuery(id+"F19.opExtrude","CAP_EDGE",EDGE,{"disambiguationData":[OSD([sQuery(id+"F0.wireOp",EDGE,"E0.bottom"),sQuery(id+"F0.wireOp",EDGE,"E0.left"),subQ0,sQuery(id+"F6.wireOp",EDGE,"E3.right")])],"isStart":false})}),makeQuery(id+"F20.opExtrude","SWEPT_EDGE",EDGE,{"disambiguationData":[OSD([subQ0,sQuery(id+"F6.wireOp",EDGE,"E3.left")])]})]});}
            var Q4;
            {var subQ0=sQuery(id+"F4.wireOp",EDGE,"E2.left");Q4=makeQuery(id+"F22.boolean.opBoolean","MERGE",EDGE,{"derivedFrom":[makeQuery(id+"F20.opExtrude","CAP_EDGE",EDGE,{"disambiguationData":[OSD([sQuery(id+"F0.wireOp",EDGE,"E0.bottom"),sQuery(id+"F0.wireOp",EDGE,"E0.left"),sQuery(id+"F4.wireOp",EDGE,"E2.top"),subQ0,sQuery(id+"F6.wireOp",EDGE,"E3.top"),sQuery(id+"F6.wireOp",EDGE,"E3.left")])],"isStart":false}),makeQuery(id+"F22.opExtrude","SWEPT_EDGE",EDGE,{"disambiguationData":[OSD([sQuery(id+"F4.wireOp",EDGE,"E2.bottom"),subQ0])]})]});}
            var Q5;
            {var subQ0=sQuery(id+"F4.wireOp",EDGE,"E2.right");var subQ1=sQuery(id+"F4.wireOp",EDGE,"E2.left");var subQ2=sQuery(id+"F4.wireOp",EDGE,"E2.bottom");var subQ3=sQuery(id+"F0.wireOp",EDGE,"E0.left");var subQ4=sQuery(id+"F0.wireOp",EDGE,"E0.bottom");var subQ5=sQuery(id+"F6.wireOp",EDGE,"E3.left");var subQ6=sQuery(id+"F6.wireOp",EDGE,"E3.top");var subQ7=sQuery(id+"F4.wireOp",EDGE,"E2.top");var subQ8=sQuery(id+"F6.wireOp",EDGE,"E3.right");var subQ9=makeQuery(id+"F3.opExtrude","SWEPT_FACE",FACE,{"disambiguationData":[OSD([subQ4,subQ3]),TDD([makeQuery(id+"F2.boolean.opBoolean","MERGE",EDGE,{"derivedFrom":[makeQuery(id+"F1.opExtrude","CAP_EDGE",EDGE,{"disambiguationData":[OSD([subQ4])],"isStart":false}),makeQuery(id+"F2.opExtrude","SWEPT_EDGE",EDGE,{"disambiguationData":[OSD([subQ4,subQ3]),TDD([makeQuery(id+"F1.opExtrude","CAP_VERTEX",VERTEX,{"disambiguationData":[OSD([subQ4,subQ3])],"isStart":false})])]})]})])]});var subQ10=makeQuery(id+"F2.opExtrude","SWEPT_FACE",FACE,{"disambiguationData":[OSD([subQ3]),TDD([makeQuery(id+"F1.opExtrude","CAP_EDGE",EDGE,{"disambiguationData":[OSD([subQ3])],"isStart":false})])]});var subQ11=makeQuery(id+"F1.opExtrude","CAP_FACE",FACE,{"disambiguationData":[OSD([subQ4,sQuery(id+"F0.wireOp",EDGE,"E0.top"),subQ3,sQuery(id+"F0.wireOp",EDGE,"E0.right")])],"isStart":false});Q5=makeQuery(id+"F25.boolean.opBoolean","INTERSECT",EDGE,{"derivedFrom":[makeQuery(id+"F22.boolean.opBoolean","MERGE",FACE,{"derivedFrom":[makeQuery(id+"F20.boolean.opBoolean","MERGE",FACE,{"derivedFrom":[makeQuery(id+"F19.boolean.opBoolean","MERGE",FACE,{"derivedFrom":[makeQuery(id+"F17.boolean.opBoolean","SPLIT",FACE,{"disambiguationData":[TD([makeQuery(id+"F2.opExtrude","CAP_FACE",FACE,{"disambiguationData":[OSD([subQ3])],"isStart":false})])],"derivedFrom":makeQuery(id+"F3.boolean.opBoolean","MERGE",FACE,{"derivedFrom":[makeQuery(id+"F2.boolean.opBoolean","MERGE",FACE,{"derivedFrom":[subQ11,subQ10]}),subQ9]})}),makeQuery(id+"F19.opExtrude","CAP_FACE",FACE,{"disambiguationData":[OSD([sQuery(id+"F6.wireOp",EDGE,"E3.bottom"),subQ6,subQ5,subQ8])],"isStart":false}),makeQuery(id+"F19.opExtrude","CAP_FACE",FACE,{"disambiguationData":[OSD([subQ2,subQ7,subQ1,subQ0])],"isStart":false})]}),makeQuery(id+"F20.opExtrude","SWEPT_FACE",FACE,{"disambiguationData":[OSD([subQ4,subQ3,subQ7,subQ1,subQ6,subQ5])]})]}),makeQuery(id+"F22.opExtrude","SWEPT_FACE",FACE,{"disambiguationData":[OSD([subQ4,subQ3,subQ2,subQ1,subQ0])]})]}),makeQuery(id+"F25.opExtrude","CAP_FACE",FACE,{"disambiguationData":[OSD([subQ4,subQ3,sQuery(id+"F4.wireOp",EDGE,"E1.bottom"),sQuery(id+"F4.wireOp",EDGE,"E1.right"),subQ2,subQ1,subQ0])],"isStart":false})]});}
            var Q6;
            {var subQ0=sQuery(id+"F0.wireOp",EDGE,"E0.left");var subQ1=sQuery(id+"F0.wireOp",EDGE,"E0.bottom");Q6=makeQuery(id+"F22.boolean.opBoolean","MERGE",FACE,{"derivedFrom":[makeQuery(id+"F20.boolean.opBoolean","MERGE",FACE,{"derivedFrom":[makeQuery(id+"F3.boolean.opBoolean","MERGE",FACE,{"derivedFrom":[makeQuery(id+"F2.boolean.opBoolean","MERGE",FACE,{"derivedFrom":[makeQuery(id+"F1.opExtrude","CAP_FACE",FACE,{"disambiguationData":[OSD([subQ1,sQuery(id+"F0.wireOp",EDGE,"E0.top"),subQ0,sQuery(id+"F0.wireOp",EDGE,"E0.right")])],"isStart":true}),makeQuery(id+"F2.opExtrude","SWEPT_FACE",FACE,{"disambiguationData":[OSD([subQ0]),TDD([makeQuery(id+"F1.opExtrude","CAP_EDGE",EDGE,{"disambiguationData":[OSD([subQ0])],"isStart":true})])]})]}),makeQuery(id+"F3.opExtrude","SWEPT_FACE",FACE,{"disambiguationData":[OSD([subQ1,subQ0]),TDD([makeQuery(id+"F2.boolean.opBoolean","MERGE",EDGE,{"derivedFrom":[makeQuery(id+"F1.opExtrude","CAP_EDGE",EDGE,{"disambiguationData":[OSD([subQ1])],"isStart":true}),makeQuery(id+"F2.opExtrude","SWEPT_EDGE",EDGE,{"disambiguationData":[OSD([subQ1,subQ0]),TDD([makeQuery(id+"F1.opExtrude","CAP_VERTEX",VERTEX,{"disambiguationData":[OSD([subQ1,subQ0])],"isStart":true})])]})]})])]})]}),makeQuery(id+"F20.opExtrude","SWEPT_FACE",FACE,{"disambiguationData":[OSD([subQ1,subQ0])]})]}),makeQuery(id+"F22.opExtrude","SWEPT_FACE",FACE,{"disambiguationData":[OSD([subQ1,subQ0])]})]});}
            chamfer(context, id + "F26", {"entities" : qUnion([Q0, Q1, Q2, Q3, Q4, Q5, Q6]), "width" : 1 * mm, "tangentPropagation" : true});
        }
    });
